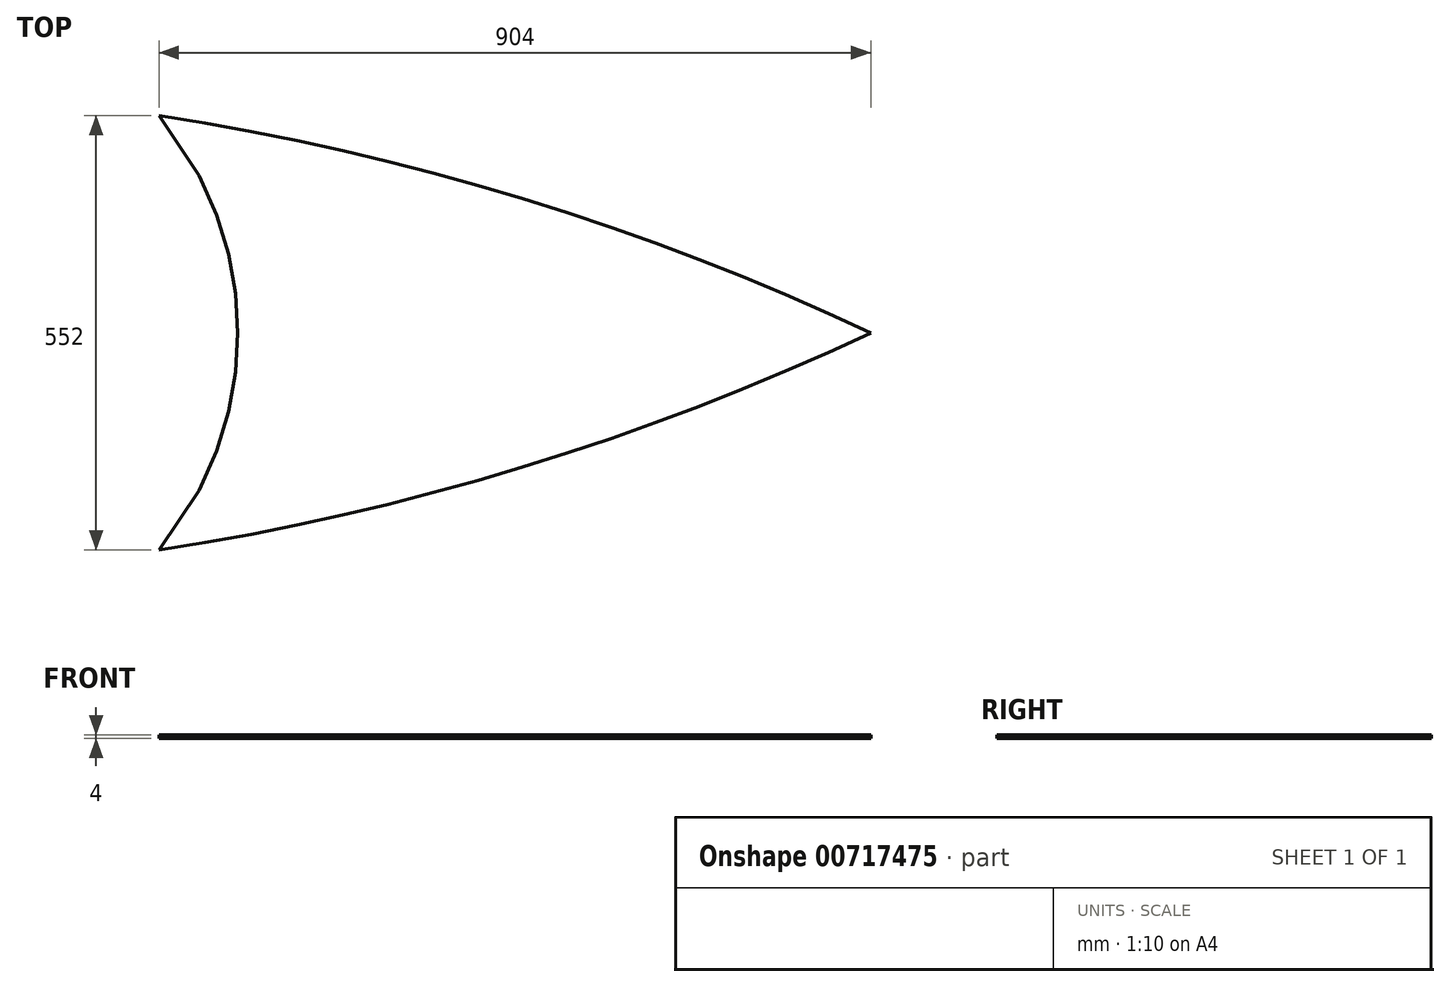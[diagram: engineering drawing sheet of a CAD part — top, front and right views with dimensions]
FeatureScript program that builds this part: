
annotation { "Feature Type Name" : "Feature", "Feature Type Description" : "" }
export const myFeature = defineFeature(function(context is Context, id is Id, definition is map)
    precondition{}
    {
        {
            var Q0;
            Q0=qCreatedBy(makeId("Top.planeOp"),FACE);
            var sketch = newSketch(context, id + "F0", { "sketchPlane" : qUnion([Q0])});
            skLineSegment(sketch, "E0", {"start": v(100, 0) * mm, "end": v(904, 0) * mm});
            skLineSegment(sketch, "E1", {"start": v(0, 276) * mm, "end": v(51, 200) * mm});
            skLineSegment(sketch, "E2", {"start": v(73, 150) * mm, "end": v(51, 200) * mm});
            skLineSegment(sketch, "E3", {"start": v(73, 150) * mm, "end": v(88, 100) * mm});
            skLineSegment(sketch, "E4", {"start": v(97, 50) * mm, "end": v(88, 100) * mm});
            skLineSegment(sketch, "E5", {"start": v(100, 0) * mm, "end": v(97, 50) * mm});
            skLineSegment(sketch, "E6.MirrorCS", {"start": v(100, 0) * mm, "end": v(97, -50) * mm});
            skLineSegment(sketch, "E7.MirrorCS", {"start": v(97, -50) * mm, "end": v(88, -100) * mm});
            skLineSegment(sketch, "E8.MirrorCS", {"start": v(0, -276) * mm, "end": v(51, -200) * mm});
            skLineSegment(sketch, "E9.MirrorCS", {"start": v(73, -150) * mm, "end": v(51, -200) * mm});
            skLineSegment(sketch, "E10.MirrorCS", {"start": v(73, -150) * mm, "end": v(88, -100) * mm});
            skArc(sketch, "E11", {"start": v(904, 0) * mm, "mid": v(461.93, 170.53) * mm, "end": v(0, 276) * mm});
            skLineSegment(sketch, "E12", {"start": v(400, 188.78) * mm, "end": v(400, -188.78) * mm});
            skLineSegment(sketch, "E13", {"start": v(300, -215.5) * mm, "end": v(300, 215.5) * mm});
            skLineSegment(sketch, "E14", {"start": v(200, -238.9) * mm, "end": v(200, 238.9) * mm});
            skLineSegment(sketch, "E15", {"start": v(100, -259.04) * mm, "end": v(100, 259.04) * mm});
            skLineSegment(sketch, "E16", {"start": v(500, -158.66) * mm, "end": v(500, 158.66) * mm});
            skLineSegment(sketch, "E17", {"start": v(600, -125.03) * mm, "end": v(600, 125.03) * mm});
            skLineSegment(sketch, "E18", {"start": v(700, -87.79) * mm, "end": v(700, 87.79) * mm});
            skLineSegment(sketch, "E19", {"start": v(800, -46.79) * mm, "end": v(800, 46.79) * mm});
            skLineSegment(sketch, "E20", {"start": v(0, -276) * mm, "end": v(800, -276) * mm, "construction": true});
            skArc(sketch, "E21", {"start": v(0, -276) * mm, "mid": v(461.93, -170.53) * mm, "end": v(904, 0) * mm});
            skPoint(sketch, "E22.orphan", {"position": v(100, -276) * mm});
            skPoint(sketch, "E23.orphan", {"position": v(200, -276) * mm});
            skPoint(sketch, "E24.orphan", {"position": v(300, -276) * mm});
            skPoint(sketch, "E25.orphan", {"position": v(400, -276) * mm});
            skPoint(sketch, "E26.orphan", {"position": v(500, -276) * mm});
            skPoint(sketch, "E27.orphan", {"position": v(600, -276) * mm});
            skPoint(sketch, "E28.orphan", {"position": v(700, -276) * mm});
            skSolve(sketch);
        }
        {
            var Q0;
            Q0 = qSketchRegion(id + "F0", true);
            extrude(context, id + "F1", {"entities" : qUnion([Q0]), "depth" : 4 * mm, "offsetDistance" : 25 * mm});
        }
    });
